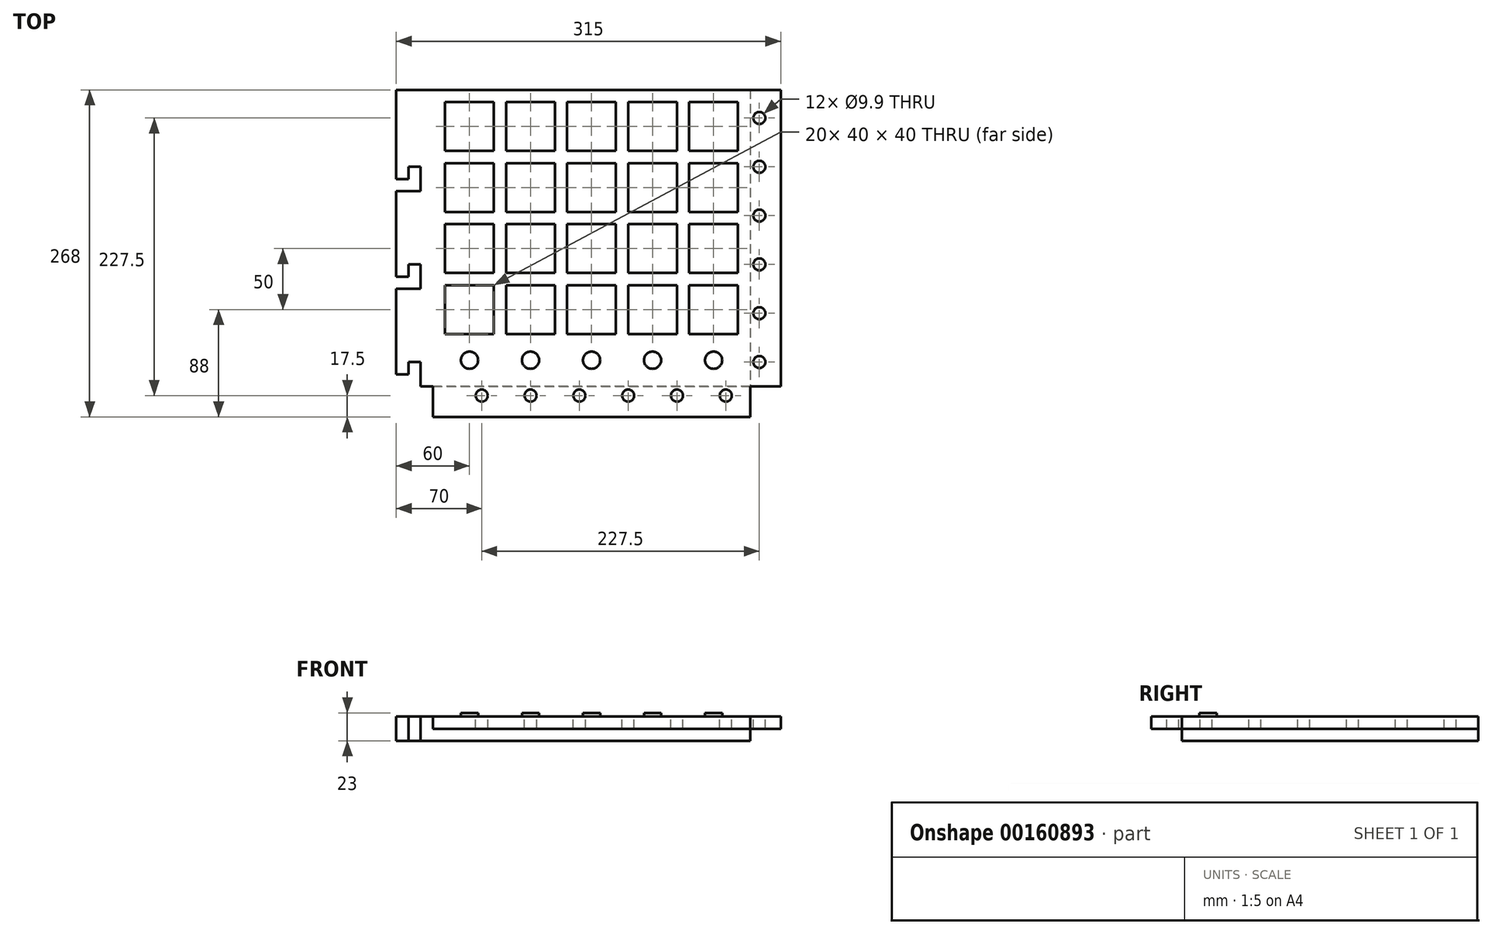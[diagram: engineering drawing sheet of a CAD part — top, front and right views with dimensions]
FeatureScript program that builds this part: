
annotation { "Feature Type Name" : "Feature", "Feature Type Description" : "" }
export const myFeature = defineFeature(function(context is Context, id is Id, definition is map)
    precondition{}
    {
        {
            var Q0;
            Q0=qCreatedBy(makeId("Top.planeOp"),FACE);
            var sketch = newSketch(context, id + "F0", { "sketchPlane" : qUnion([Q0])});
            skLineSegment(sketch, "E0", {"start": v(-205.43, 0) * mm, "end": v(243.02, 0) * mm, "construction": true});
            skLineSegment(sketch, "E1", {"start": v(0, 205.1) * mm, "end": v(0, -211.65) * mm, "construction": true});
            skLineSegment(sketch, "E2.bottom", {"start": v(130, 105) * mm, "end": v(-130, 105) * mm});
            skLineSegment(sketch, "E2.top", {"start": v(130, -105) * mm, "end": v(-130, -105) * mm});
            skLineSegment(sketch, "E2.left", {"start": v(130, 105) * mm, "end": v(130, -105) * mm});
            skLineSegment(sketch, "E2.right", {"start": v(-130, 105) * mm, "end": v(-130, -105) * mm});
            skPoint(sketch, "E2.middle", {"position": v(0, 0) * mm});
            skLineSegment(sketch, "E3.bottom", {"start": v(80, -55) * mm, "end": v(120, -55) * mm});
            skLineSegment(sketch, "E3.top", {"start": v(80, -95) * mm, "end": v(120, -95) * mm});
            skLineSegment(sketch, "E3.left", {"start": v(80, -55) * mm, "end": v(80, -95) * mm});
            skLineSegment(sketch, "E3.right", {"start": v(120, -55) * mm, "end": v(120, -95) * mm});
            skLineSegment(sketch, "E4.0.1.0", {"start": v(80, -5) * mm, "end": v(120, -5) * mm});
            skLineSegment(sketch, "E4.0.1.1", {"start": v(120, -5) * mm, "end": v(120, -45) * mm});
            skLineSegment(sketch, "E4.0.1.2", {"start": v(80, -45) * mm, "end": v(120, -45) * mm});
            skLineSegment(sketch, "E4.0.1.3", {"start": v(80, -5) * mm, "end": v(80, -45) * mm});
            skLineSegment(sketch, "E4.0.2.0", {"start": v(80, 45) * mm, "end": v(120, 45) * mm});
            skLineSegment(sketch, "E4.0.2.1", {"start": v(120, 45) * mm, "end": v(120, 5) * mm});
            skLineSegment(sketch, "E4.0.2.2", {"start": v(80, 5) * mm, "end": v(120, 5) * mm});
            skLineSegment(sketch, "E4.0.2.3", {"start": v(80, 45) * mm, "end": v(80, 5) * mm});
            skLineSegment(sketch, "E4.0.3.0", {"start": v(80, 95) * mm, "end": v(120, 95) * mm});
            skLineSegment(sketch, "E4.0.3.1", {"start": v(120, 95) * mm, "end": v(120, 55) * mm});
            skLineSegment(sketch, "E4.0.3.2", {"start": v(80, 55) * mm, "end": v(120, 55) * mm});
            skLineSegment(sketch, "E4.0.3.3", {"start": v(80, 95) * mm, "end": v(80, 55) * mm});
            skLineSegment(sketch, "E4.1.0.0", {"start": v(30, -55) * mm, "end": v(70, -55) * mm});
            skLineSegment(sketch, "E4.1.0.1", {"start": v(70, -55) * mm, "end": v(70, -95) * mm});
            skLineSegment(sketch, "E4.1.0.2", {"start": v(30, -95) * mm, "end": v(70, -95) * mm});
            skLineSegment(sketch, "E4.1.0.3", {"start": v(30, -55) * mm, "end": v(30, -95) * mm});
            skLineSegment(sketch, "E4.1.1.0", {"start": v(30, -5) * mm, "end": v(70, -5) * mm});
            skLineSegment(sketch, "E4.1.1.1", {"start": v(70, -5) * mm, "end": v(70, -45) * mm});
            skLineSegment(sketch, "E4.1.1.2", {"start": v(30, -45) * mm, "end": v(70, -45) * mm});
            skLineSegment(sketch, "E4.1.1.3", {"start": v(30, -5) * mm, "end": v(30, -45) * mm});
            skLineSegment(sketch, "E4.1.2.0", {"start": v(30, 45) * mm, "end": v(70, 45) * mm});
            skLineSegment(sketch, "E4.1.2.1", {"start": v(70, 45) * mm, "end": v(70, 5) * mm});
            skLineSegment(sketch, "E4.1.2.2", {"start": v(30, 5) * mm, "end": v(70, 5) * mm});
            skLineSegment(sketch, "E4.1.2.3", {"start": v(30, 45) * mm, "end": v(30, 5) * mm});
            skLineSegment(sketch, "E4.1.3.0", {"start": v(30, 95) * mm, "end": v(70, 95) * mm});
            skLineSegment(sketch, "E4.1.3.1", {"start": v(70, 95) * mm, "end": v(70, 55) * mm});
            skLineSegment(sketch, "E4.1.3.2", {"start": v(30, 55) * mm, "end": v(70, 55) * mm});
            skLineSegment(sketch, "E4.1.3.3", {"start": v(30, 95) * mm, "end": v(30, 55) * mm});
            skLineSegment(sketch, "E4.2.0.0", {"start": v(-20, -55) * mm, "end": v(20, -55) * mm});
            skLineSegment(sketch, "E4.2.0.1", {"start": v(20, -55) * mm, "end": v(20, -95) * mm});
            skLineSegment(sketch, "E4.2.0.2", {"start": v(-20, -95) * mm, "end": v(20, -95) * mm});
            skLineSegment(sketch, "E4.2.0.3", {"start": v(-20, -55) * mm, "end": v(-20, -95) * mm});
            skLineSegment(sketch, "E4.2.1.0", {"start": v(-20, -5) * mm, "end": v(20, -5) * mm});
            skLineSegment(sketch, "E4.2.1.1", {"start": v(20, -5) * mm, "end": v(20, -45) * mm});
            skLineSegment(sketch, "E4.2.1.2", {"start": v(-20, -45) * mm, "end": v(20, -45) * mm});
            skLineSegment(sketch, "E4.2.1.3", {"start": v(-20, -5) * mm, "end": v(-20, -45) * mm});
            skLineSegment(sketch, "E4.2.2.0", {"start": v(-20, 45) * mm, "end": v(20, 45) * mm});
            skLineSegment(sketch, "E4.2.2.1", {"start": v(20, 45) * mm, "end": v(20, 5) * mm});
            skLineSegment(sketch, "E4.2.2.2", {"start": v(-20, 5) * mm, "end": v(20, 5) * mm});
            skLineSegment(sketch, "E4.2.2.3", {"start": v(-20, 45) * mm, "end": v(-20, 5) * mm});
            skLineSegment(sketch, "E4.2.3.0", {"start": v(-20, 95) * mm, "end": v(20, 95) * mm});
            skLineSegment(sketch, "E4.2.3.1", {"start": v(20, 95) * mm, "end": v(20, 55) * mm});
            skLineSegment(sketch, "E4.2.3.2", {"start": v(-20, 55) * mm, "end": v(20, 55) * mm});
            skLineSegment(sketch, "E4.2.3.3", {"start": v(-20, 95) * mm, "end": v(-20, 55) * mm});
            skLineSegment(sketch, "E4.3.0.0", {"start": v(-70, -55) * mm, "end": v(-30, -55) * mm});
            skLineSegment(sketch, "E4.3.0.1", {"start": v(-30, -55) * mm, "end": v(-30, -95) * mm});
            skLineSegment(sketch, "E4.3.0.2", {"start": v(-70, -95) * mm, "end": v(-30, -95) * mm});
            skLineSegment(sketch, "E4.3.0.3", {"start": v(-70, -55) * mm, "end": v(-70, -95) * mm});
            skLineSegment(sketch, "E4.3.1.0", {"start": v(-70, -5) * mm, "end": v(-30, -5) * mm});
            skLineSegment(sketch, "E4.3.1.1", {"start": v(-30, -5) * mm, "end": v(-30, -45) * mm});
            skLineSegment(sketch, "E4.3.1.2", {"start": v(-70, -45) * mm, "end": v(-30, -45) * mm});
            skLineSegment(sketch, "E4.3.1.3", {"start": v(-70, -5) * mm, "end": v(-70, -45) * mm});
            skLineSegment(sketch, "E4.3.2.0", {"start": v(-70, 45) * mm, "end": v(-30, 45) * mm});
            skLineSegment(sketch, "E4.3.2.1", {"start": v(-30, 45) * mm, "end": v(-30, 5) * mm});
            skLineSegment(sketch, "E4.3.2.2", {"start": v(-70, 5) * mm, "end": v(-30, 5) * mm});
            skLineSegment(sketch, "E4.3.2.3", {"start": v(-70, 45) * mm, "end": v(-70, 5) * mm});
            skLineSegment(sketch, "E4.3.3.0", {"start": v(-70, 95) * mm, "end": v(-30, 95) * mm});
            skLineSegment(sketch, "E4.3.3.1", {"start": v(-30, 95) * mm, "end": v(-30, 55) * mm});
            skLineSegment(sketch, "E4.3.3.2", {"start": v(-70, 55) * mm, "end": v(-30, 55) * mm});
            skLineSegment(sketch, "E4.3.3.3", {"start": v(-70, 95) * mm, "end": v(-70, 55) * mm});
            skLineSegment(sketch, "E4.4.0.0", {"start": v(-120, -55) * mm, "end": v(-80, -55) * mm});
            skLineSegment(sketch, "E4.4.0.1", {"start": v(-80, -55) * mm, "end": v(-80, -95) * mm});
            skLineSegment(sketch, "E4.4.0.2", {"start": v(-120, -95) * mm, "end": v(-80, -95) * mm});
            skLineSegment(sketch, "E4.4.0.3", {"start": v(-120, -55) * mm, "end": v(-120, -95) * mm});
            skLineSegment(sketch, "E4.4.1.0", {"start": v(-120, -5) * mm, "end": v(-80, -5) * mm});
            skLineSegment(sketch, "E4.4.1.1", {"start": v(-80, -5) * mm, "end": v(-80, -45) * mm});
            skLineSegment(sketch, "E4.4.1.2", {"start": v(-120, -45) * mm, "end": v(-80, -45) * mm});
            skLineSegment(sketch, "E4.4.1.3", {"start": v(-120, -5) * mm, "end": v(-120, -45) * mm});
            skLineSegment(sketch, "E4.4.2.0", {"start": v(-120, 45) * mm, "end": v(-80, 45) * mm});
            skLineSegment(sketch, "E4.4.2.1", {"start": v(-80, 45) * mm, "end": v(-80, 5) * mm});
            skLineSegment(sketch, "E4.4.2.2", {"start": v(-120, 5) * mm, "end": v(-80, 5) * mm});
            skLineSegment(sketch, "E4.4.2.3", {"start": v(-120, 45) * mm, "end": v(-120, 5) * mm});
            skLineSegment(sketch, "E4.4.3.0", {"start": v(-120, 95) * mm, "end": v(-80, 95) * mm});
            skLineSegment(sketch, "E4.4.3.1", {"start": v(-80, 95) * mm, "end": v(-80, 55) * mm});
            skLineSegment(sketch, "E4.4.3.2", {"start": v(-120, 55) * mm, "end": v(-80, 55) * mm});
            skLineSegment(sketch, "E4.4.3.3", {"start": v(-120, 95) * mm, "end": v(-120, 55) * mm});
            skLineSegment(sketch, "E4.direction1", {"start": v(80, -95) * mm, "end": v(30, -95) * mm, "construction": true});
            skLineSegment(sketch, "E4.direction2", {"start": v(80, -95) * mm, "end": v(80, -45) * mm, "construction": true});
            skSolve(sketch);
        }
        {
            var Q0;
            Q0 = qSketchRegion(id + "F0", true);
            extrude(context, id + "F1", {"entities" : qUnion([Q0]), "depth" : 20 * mm});
        }
        {
            var Q0;
            Q0=makeQuery(id+"F1.opExtrude","SWEPT_FACE",FACE,{"disambiguationData":[OSD([sQuery(id+"F0.wireOp",EDGE,"E2.top")])]});
            extrude(context, id + "F2", {"entities" : qUnion([Q0]), "operationType" : NewBodyOperationType.ADD, "depth" : 33 * mm});
        }
        {
            var Q0;
            Q0=makeQuery(id+"F2.opExtrude","CAP_FACE",FACE,{"disambiguationData":[OSD([sQuery(id+"F0.wireOp",EDGE,"E2.top")])],"isStart":false});
            var sketch = newSketch(context, id + "F3", { "sketchPlane" : qUnion([Q0])});
            skLineSegment(sketch, "E5.bottom", {"start": v(-130, 20) * mm, "end": v(130, 20) * mm});
            skLineSegment(sketch, "E5.top", {"start": v(-130, 10) * mm, "end": v(130, 10) * mm});
            skLineSegment(sketch, "E5.left", {"start": v(-130, 20) * mm, "end": v(-130, 10) * mm});
            skLineSegment(sketch, "E5.right", {"start": v(130, 20) * mm, "end": v(130, 10) * mm});
            skSolve(sketch);
        }
        {
            var Q0;
            Q0 = qSketchRegion(id + "F3", true);
            extrude(context, id + "F4", {"entities" : qUnion([Q0]), "operationType" : NewBodyOperationType.ADD, "depth" : 25 * mm});
        }
        {
            var Q0;
            {var subQ0=sQuery(id+"F0.wireOp",EDGE,"E2.top");Q0=makeQuery(id+"F4.boolean.opBoolean","MERGE",FACE,{"derivedFrom":[makeQuery(id+"F2.boolean.opBoolean","MERGE",FACE,{"derivedFrom":[makeQuery(id+"F1.opExtrude","CAP_FACE",FACE,{"disambiguationData":[OSD([sQuery(id+"F0.wireOp",EDGE,"E2.bottom"),subQ0,sQuery(id+"F0.wireOp",EDGE,"E2.left"),sQuery(id+"F0.wireOp",EDGE,"E2.right"),sQuery(id+"F0.wireOp",EDGE,"E3.bottom"),sQuery(id+"F0.wireOp",EDGE,"E3.top"),sQuery(id+"F0.wireOp",EDGE,"E3.left"),sQuery(id+"F0.wireOp",EDGE,"E3.right"),sQuery(id+"F0.wireOp",EDGE,"E4.0.1.0"),sQuery(id+"F0.wireOp",EDGE,"E4.0.1.1"),sQuery(id+"F0.wireOp",EDGE,"E4.0.1.2"),sQuery(id+"F0.wireOp",EDGE,"E4.0.1.3"),sQuery(id+"F0.wireOp",EDGE,"E4.0.2.0"),sQuery(id+"F0.wireOp",EDGE,"E4.0.2.1"),sQuery(id+"F0.wireOp",EDGE,"E4.0.2.2"),sQuery(id+"F0.wireOp",EDGE,"E4.0.2.3"),sQuery(id+"F0.wireOp",EDGE,"E4.0.3.0"),sQuery(id+"F0.wireOp",EDGE,"E4.0.3.1"),sQuery(id+"F0.wireOp",EDGE,"E4.0.3.2"),sQuery(id+"F0.wireOp",EDGE,"E4.0.3.3"),sQuery(id+"F0.wireOp",EDGE,"E4.1.0.0"),sQuery(id+"F0.wireOp",EDGE,"E4.1.0.1"),sQuery(id+"F0.wireOp",EDGE,"E4.1.0.2"),sQuery(id+"F0.wireOp",EDGE,"E4.1.0.3"),sQuery(id+"F0.wireOp",EDGE,"E4.1.1.0"),sQuery(id+"F0.wireOp",EDGE,"E4.1.1.1"),sQuery(id+"F0.wireOp",EDGE,"E4.1.1.2"),sQuery(id+"F0.wireOp",EDGE,"E4.1.1.3"),sQuery(id+"F0.wireOp",EDGE,"E4.1.2.0"),sQuery(id+"F0.wireOp",EDGE,"E4.1.2.1"),sQuery(id+"F0.wireOp",EDGE,"E4.1.2.2"),sQuery(id+"F0.wireOp",EDGE,"E4.1.2.3"),sQuery(id+"F0.wireOp",EDGE,"E4.1.3.0"),sQuery(id+"F0.wireOp",EDGE,"E4.1.3.1"),sQuery(id+"F0.wireOp",EDGE,"E4.1.3.2"),sQuery(id+"F0.wireOp",EDGE,"E4.1.3.3"),sQuery(id+"F0.wireOp",EDGE,"E4.2.0.0"),sQuery(id+"F0.wireOp",EDGE,"E4.2.0.1"),sQuery(id+"F0.wireOp",EDGE,"E4.2.0.2"),sQuery(id+"F0.wireOp",EDGE,"E4.2.0.3"),sQuery(id+"F0.wireOp",EDGE,"E4.2.1.0"),sQuery(id+"F0.wireOp",EDGE,"E4.2.1.1"),sQuery(id+"F0.wireOp",EDGE,"E4.2.1.2"),sQuery(id+"F0.wireOp",EDGE,"E4.2.1.3"),sQuery(id+"F0.wireOp",EDGE,"E4.2.2.0"),sQuery(id+"F0.wireOp",EDGE,"E4.2.2.1"),sQuery(id+"F0.wireOp",EDGE,"E4.2.2.2"),sQuery(id+"F0.wireOp",EDGE,"E4.2.2.3"),sQuery(id+"F0.wireOp",EDGE,"E4.2.3.0"),sQuery(id+"F0.wireOp",EDGE,"E4.2.3.1"),sQuery(id+"F0.wireOp",EDGE,"E4.2.3.2"),sQuery(id+"F0.wireOp",EDGE,"E4.2.3.3"),sQuery(id+"F0.wireOp",EDGE,"E4.3.0.0"),sQuery(id+"F0.wireOp",EDGE,"E4.3.0.1"),sQuery(id+"F0.wireOp",EDGE,"E4.3.0.2"),sQuery(id+"F0.wireOp",EDGE,"E4.3.0.3"),sQuery(id+"F0.wireOp",EDGE,"E4.3.1.0"),sQuery(id+"F0.wireOp",EDGE,"E4.3.1.1"),sQuery(id+"F0.wireOp",EDGE,"E4.3.1.2"),sQuery(id+"F0.wireOp",EDGE,"E4.3.1.3"),sQuery(id+"F0.wireOp",EDGE,"E4.3.2.0"),sQuery(id+"F0.wireOp",EDGE,"E4.3.2.1"),sQuery(id+"F0.wireOp",EDGE,"E4.3.2.2"),sQuery(id+"F0.wireOp",EDGE,"E4.3.2.3"),sQuery(id+"F0.wireOp",EDGE,"E4.3.3.0"),sQuery(id+"F0.wireOp",EDGE,"E4.3.3.1"),sQuery(id+"F0.wireOp",EDGE,"E4.3.3.2"),sQuery(id+"F0.wireOp",EDGE,"E4.3.3.3"),sQuery(id+"F0.wireOp",EDGE,"E4.4.0.0"),sQuery(id+"F0.wireOp",EDGE,"E4.4.0.1"),sQuery(id+"F0.wireOp",EDGE,"E4.4.0.2"),sQuery(id+"F0.wireOp",EDGE,"E4.4.0.3"),sQuery(id+"F0.wireOp",EDGE,"E4.4.1.0"),sQuery(id+"F0.wireOp",EDGE,"E4.4.1.1"),sQuery(id+"F0.wireOp",EDGE,"E4.4.1.2"),sQuery(id+"F0.wireOp",EDGE,"E4.4.1.3"),sQuery(id+"F0.wireOp",EDGE,"E4.4.2.0"),sQuery(id+"F0.wireOp",EDGE,"E4.4.2.1"),sQuery(id+"F0.wireOp",EDGE,"E4.4.2.2"),sQuery(id+"F0.wireOp",EDGE,"E4.4.2.3"),sQuery(id+"F0.wireOp",EDGE,"E4.4.3.0"),sQuery(id+"F0.wireOp",EDGE,"E4.4.3.1"),sQuery(id+"F0.wireOp",EDGE,"E4.4.3.2"),sQuery(id+"F0.wireOp",EDGE,"E4.4.3.3")])],"isStart":false}),makeQuery(id+"F2.opExtrude","SWEPT_FACE",FACE,{"disambiguationData":[OSD([subQ0]),TDD([makeQuery(id+"F1.opExtrude","CAP_EDGE",EDGE,{"disambiguationData":[OSD([subQ0])],"isStart":false})])]})]}),makeQuery(id+"F4.opExtrude","SWEPT_FACE",FACE,{"disambiguationData":[OSD([sQuery(id+"F3.wireOp",EDGE,"E5.bottom")])]})]});}
            var sketch = newSketch(context, id + "F5", { "sketchPlane" : qUnion([Q0])});
            skCircle(sketch, "E6", {"center": v(110, -145.5) * mm, "radius": 4.95 * mm});
            skLineSegment(sketch, "E7", {"start": v(-121.54, -145.5) * mm, "end": v(178.6, -145.5) * mm, "construction": true});
            skLineSegment(sketch, "E8", {"start": v(110, -159.43) * mm, "end": v(110, -131.93) * mm, "construction": true});
            skCircle(sketch, "E9.1.0.0", {"center": v(70, -145.5) * mm, "radius": 4.95 * mm});
            skCircle(sketch, "E9.2.0.0", {"center": v(30, -145.5) * mm, "radius": 4.95 * mm});
            skCircle(sketch, "E9.3.0.0", {"center": v(-10, -145.5) * mm, "radius": 4.95 * mm});
            skCircle(sketch, "E9.4.0.0", {"center": v(-50, -145.5) * mm, "radius": 4.95 * mm});
            skCircle(sketch, "E9.5.0.0", {"center": v(-90, -145.5) * mm, "radius": 4.95 * mm});
            skLineSegment(sketch, "E9.direction1", {"start": v(110, -145.5) * mm, "end": v(70, -145.5) * mm, "construction": true});
            skSolve(sketch);
        }
        {
            var Q0;
            Q0 = qSketchRegion(id + "F5", true);
            extrude(context, id + "F6", {"entities" : qUnion([Q0]), "operationType" : NewBodyOperationType.REMOVE, "oppositeDirection" : true, "depth" : 25 * mm});
        }
        {
            var Q0;
            {var subQ0=sQuery(id+"F0.wireOp",EDGE,"E2.left");Q0=makeQuery(id+"F4.boolean.opBoolean","MERGE",FACE,{"derivedFrom":[makeQuery(id+"F2.boolean.opBoolean","MERGE",FACE,{"derivedFrom":[makeQuery(id+"F1.opExtrude","SWEPT_FACE",FACE,{"disambiguationData":[OSD([subQ0])]}),makeQuery(id+"F2.opExtrude","SWEPT_FACE",FACE,{"disambiguationData":[OSD([sQuery(id+"F0.wireOp",EDGE,"E2.top"),subQ0])]})]}),makeQuery(id+"F4.opExtrude","SWEPT_FACE",FACE,{"disambiguationData":[OSD([sQuery(id+"F3.wireOp",EDGE,"E5.right")])]})]});}
            var sketch = newSketch(context, id + "F7", { "sketchPlane" : qUnion([Q0])});
            skLineSegment(sketch, "E10.bottom", {"start": v(105, 20) * mm, "end": v(-138, 20) * mm});
            skLineSegment(sketch, "E10.top", {"start": v(105, 10) * mm, "end": v(-138, 10) * mm});
            skLineSegment(sketch, "E10.left", {"start": v(105, 20) * mm, "end": v(105, 10) * mm});
            skLineSegment(sketch, "E10.right", {"start": v(-138, 20) * mm, "end": v(-138, 10) * mm});
            skSolve(sketch);
        }
        {
            var Q0;
            Q0 = qSketchRegion(id + "F7", true);
            extrude(context, id + "F8", {"entities" : qUnion([Q0]), "operationType" : NewBodyOperationType.ADD, "depth" : 25 * mm});
        }
        {
            var Q0;
            {var subQ0=sQuery(id+"F0.wireOp",EDGE,"E2.top");Q0=makeQuery(id+"F8.boolean.opBoolean","MERGE",FACE,{"derivedFrom":[makeQuery(id+"F4.boolean.opBoolean","MERGE",FACE,{"derivedFrom":[makeQuery(id+"F2.boolean.opBoolean","MERGE",FACE,{"derivedFrom":[makeQuery(id+"F1.opExtrude","CAP_FACE",FACE,{"disambiguationData":[OSD([sQuery(id+"F0.wireOp",EDGE,"E2.bottom"),subQ0,sQuery(id+"F0.wireOp",EDGE,"E2.left"),sQuery(id+"F0.wireOp",EDGE,"E2.right"),sQuery(id+"F0.wireOp",EDGE,"E3.bottom"),sQuery(id+"F0.wireOp",EDGE,"E3.top"),sQuery(id+"F0.wireOp",EDGE,"E3.left"),sQuery(id+"F0.wireOp",EDGE,"E3.right"),sQuery(id+"F0.wireOp",EDGE,"E4.0.1.0"),sQuery(id+"F0.wireOp",EDGE,"E4.0.1.1"),sQuery(id+"F0.wireOp",EDGE,"E4.0.1.2"),sQuery(id+"F0.wireOp",EDGE,"E4.0.1.3"),sQuery(id+"F0.wireOp",EDGE,"E4.0.2.0"),sQuery(id+"F0.wireOp",EDGE,"E4.0.2.1"),sQuery(id+"F0.wireOp",EDGE,"E4.0.2.2"),sQuery(id+"F0.wireOp",EDGE,"E4.0.2.3"),sQuery(id+"F0.wireOp",EDGE,"E4.0.3.0"),sQuery(id+"F0.wireOp",EDGE,"E4.0.3.1"),sQuery(id+"F0.wireOp",EDGE,"E4.0.3.2"),sQuery(id+"F0.wireOp",EDGE,"E4.0.3.3"),sQuery(id+"F0.wireOp",EDGE,"E4.1.0.0"),sQuery(id+"F0.wireOp",EDGE,"E4.1.0.1"),sQuery(id+"F0.wireOp",EDGE,"E4.1.0.2"),sQuery(id+"F0.wireOp",EDGE,"E4.1.0.3"),sQuery(id+"F0.wireOp",EDGE,"E4.1.1.0"),sQuery(id+"F0.wireOp",EDGE,"E4.1.1.1"),sQuery(id+"F0.wireOp",EDGE,"E4.1.1.2"),sQuery(id+"F0.wireOp",EDGE,"E4.1.1.3"),sQuery(id+"F0.wireOp",EDGE,"E4.1.2.0"),sQuery(id+"F0.wireOp",EDGE,"E4.1.2.1"),sQuery(id+"F0.wireOp",EDGE,"E4.1.2.2"),sQuery(id+"F0.wireOp",EDGE,"E4.1.2.3"),sQuery(id+"F0.wireOp",EDGE,"E4.1.3.0"),sQuery(id+"F0.wireOp",EDGE,"E4.1.3.1"),sQuery(id+"F0.wireOp",EDGE,"E4.1.3.2"),sQuery(id+"F0.wireOp",EDGE,"E4.1.3.3"),sQuery(id+"F0.wireOp",EDGE,"E4.2.0.0"),sQuery(id+"F0.wireOp",EDGE,"E4.2.0.1"),sQuery(id+"F0.wireOp",EDGE,"E4.2.0.2"),sQuery(id+"F0.wireOp",EDGE,"E4.2.0.3"),sQuery(id+"F0.wireOp",EDGE,"E4.2.1.0"),sQuery(id+"F0.wireOp",EDGE,"E4.2.1.1"),sQuery(id+"F0.wireOp",EDGE,"E4.2.1.2"),sQuery(id+"F0.wireOp",EDGE,"E4.2.1.3"),sQuery(id+"F0.wireOp",EDGE,"E4.2.2.0"),sQuery(id+"F0.wireOp",EDGE,"E4.2.2.1"),sQuery(id+"F0.wireOp",EDGE,"E4.2.2.2"),sQuery(id+"F0.wireOp",EDGE,"E4.2.2.3"),sQuery(id+"F0.wireOp",EDGE,"E4.2.3.0"),sQuery(id+"F0.wireOp",EDGE,"E4.2.3.1"),sQuery(id+"F0.wireOp",EDGE,"E4.2.3.2"),sQuery(id+"F0.wireOp",EDGE,"E4.2.3.3"),sQuery(id+"F0.wireOp",EDGE,"E4.3.0.0"),sQuery(id+"F0.wireOp",EDGE,"E4.3.0.1"),sQuery(id+"F0.wireOp",EDGE,"E4.3.0.2"),sQuery(id+"F0.wireOp",EDGE,"E4.3.0.3"),sQuery(id+"F0.wireOp",EDGE,"E4.3.1.0"),sQuery(id+"F0.wireOp",EDGE,"E4.3.1.1"),sQuery(id+"F0.wireOp",EDGE,"E4.3.1.2"),sQuery(id+"F0.wireOp",EDGE,"E4.3.1.3"),sQuery(id+"F0.wireOp",EDGE,"E4.3.2.0"),sQuery(id+"F0.wireOp",EDGE,"E4.3.2.1"),sQuery(id+"F0.wireOp",EDGE,"E4.3.2.2"),sQuery(id+"F0.wireOp",EDGE,"E4.3.2.3"),sQuery(id+"F0.wireOp",EDGE,"E4.3.3.0"),sQuery(id+"F0.wireOp",EDGE,"E4.3.3.1"),sQuery(id+"F0.wireOp",EDGE,"E4.3.3.2"),sQuery(id+"F0.wireOp",EDGE,"E4.3.3.3"),sQuery(id+"F0.wireOp",EDGE,"E4.4.0.0"),sQuery(id+"F0.wireOp",EDGE,"E4.4.0.1"),sQuery(id+"F0.wireOp",EDGE,"E4.4.0.2"),sQuery(id+"F0.wireOp",EDGE,"E4.4.0.3"),sQuery(id+"F0.wireOp",EDGE,"E4.4.1.0"),sQuery(id+"F0.wireOp",EDGE,"E4.4.1.1"),sQuery(id+"F0.wireOp",EDGE,"E4.4.1.2"),sQuery(id+"F0.wireOp",EDGE,"E4.4.1.3"),sQuery(id+"F0.wireOp",EDGE,"E4.4.2.0"),sQuery(id+"F0.wireOp",EDGE,"E4.4.2.1"),sQuery(id+"F0.wireOp",EDGE,"E4.4.2.2"),sQuery(id+"F0.wireOp",EDGE,"E4.4.2.3"),sQuery(id+"F0.wireOp",EDGE,"E4.4.3.0"),sQuery(id+"F0.wireOp",EDGE,"E4.4.3.1"),sQuery(id+"F0.wireOp",EDGE,"E4.4.3.2"),sQuery(id+"F0.wireOp",EDGE,"E4.4.3.3")])],"isStart":false}),makeQuery(id+"F2.opExtrude","SWEPT_FACE",FACE,{"disambiguationData":[OSD([subQ0]),TDD([makeQuery(id+"F1.opExtrude","CAP_EDGE",EDGE,{"disambiguationData":[OSD([subQ0])],"isStart":false})])]})]}),makeQuery(id+"F4.opExtrude","SWEPT_FACE",FACE,{"disambiguationData":[OSD([sQuery(id+"F3.wireOp",EDGE,"E5.bottom")])]})]}),makeQuery(id+"F8.opExtrude","SWEPT_FACE",FACE,{"disambiguationData":[OSD([sQuery(id+"F7.wireOp",EDGE,"E10.bottom")])]})]});}
            var sketch = newSketch(context, id + "F9", { "sketchPlane" : qUnion([Q0])});
            skLineSegment(sketch, "E11", {"start": v(137.5, -148.15) * mm, "end": v(137.5, 118.27) * mm, "construction": true});
            skCircle(sketch, "E12", {"center": v(137.5, -118) * mm, "radius": 4.95 * mm});
            skLineSegment(sketch, "E13", {"start": v(128.57, -118) * mm, "end": v(148.12, -118) * mm, "construction": true});
            skCircle(sketch, "E14.0.1.0", {"center": v(137.5, -78) * mm, "radius": 4.95 * mm});
            skCircle(sketch, "E14.0.2.0", {"center": v(137.5, -38) * mm, "radius": 4.95 * mm});
            skCircle(sketch, "E14.0.3.0", {"center": v(137.5, 2) * mm, "radius": 4.95 * mm});
            skCircle(sketch, "E14.0.4.0", {"center": v(137.5, 42) * mm, "radius": 4.95 * mm});
            skCircle(sketch, "E14.0.5.0", {"center": v(137.5, 82) * mm, "radius": 4.95 * mm});
            skLineSegment(sketch, "E14.direction1", {"start": v(137.5, -118) * mm, "end": v(150.25, -118) * mm, "construction": true});
            skLineSegment(sketch, "E14.direction2", {"start": v(137.5, -118) * mm, "end": v(137.5, -78) * mm, "construction": true});
            skSolve(sketch);
        }
        {
            var Q0;
            Q0 = qSketchRegion(id + "F9", true);
            extrude(context, id + "F10", {"entities" : qUnion([Q0]), "operationType" : NewBodyOperationType.REMOVE, "oppositeDirection" : true, "depth" : 25 * mm});
        }
        {
            var Q0;
            {var subQ0=sQuery(id+"F0.wireOp",EDGE,"E2.right");Q0=makeQuery(id+"F4.boolean.opBoolean","MERGE",FACE,{"derivedFrom":[makeQuery(id+"F2.boolean.opBoolean","MERGE",FACE,{"derivedFrom":[makeQuery(id+"F1.opExtrude","SWEPT_FACE",FACE,{"disambiguationData":[OSD([subQ0])]}),makeQuery(id+"F2.opExtrude","SWEPT_FACE",FACE,{"disambiguationData":[OSD([sQuery(id+"F0.wireOp",EDGE,"E2.top"),subQ0])]})]}),makeQuery(id+"F4.opExtrude","SWEPT_FACE",FACE,{"disambiguationData":[OSD([sQuery(id+"F3.wireOp",EDGE,"E5.left")])]})]});}
            var sketch = newSketch(context, id + "F11", { "sketchPlane" : qUnion([Q0])});
            skLineSegment(sketch, "E15.bottom", {"start": v(-105, 20) * mm, "end": v(138, 20) * mm});
            skLineSegment(sketch, "E15.top", {"start": v(-105, 0) * mm, "end": v(138, 0) * mm});
            skLineSegment(sketch, "E15.left", {"start": v(-105, 20) * mm, "end": v(-105, 0) * mm});
            skLineSegment(sketch, "E15.right", {"start": v(138, 20) * mm, "end": v(138, 0) * mm});
            skSolve(sketch);
        }
        {
            var Q0;
            Q0 = qSketchRegion(id + "F11", true);
            extrude(context, id + "F12", {"entities" : qUnion([Q0]), "operationType" : NewBodyOperationType.ADD, "depth" : 30 * mm});
        }
        {
            var Q0;
            {var subQ0=sQuery(id+"F0.wireOp",EDGE,"E2.top");Q0=makeQuery(id+"F12.boolean.opBoolean","MERGE",FACE,{"derivedFrom":[makeQuery(id+"F8.boolean.opBoolean","MERGE",FACE,{"derivedFrom":[makeQuery(id+"F4.boolean.opBoolean","MERGE",FACE,{"derivedFrom":[makeQuery(id+"F2.boolean.opBoolean","MERGE",FACE,{"derivedFrom":[makeQuery(id+"F1.opExtrude","CAP_FACE",FACE,{"disambiguationData":[OSD([sQuery(id+"F0.wireOp",EDGE,"E2.bottom"),subQ0,sQuery(id+"F0.wireOp",EDGE,"E2.left"),sQuery(id+"F0.wireOp",EDGE,"E2.right"),sQuery(id+"F0.wireOp",EDGE,"E3.bottom"),sQuery(id+"F0.wireOp",EDGE,"E3.top"),sQuery(id+"F0.wireOp",EDGE,"E3.left"),sQuery(id+"F0.wireOp",EDGE,"E3.right"),sQuery(id+"F0.wireOp",EDGE,"E4.0.1.0"),sQuery(id+"F0.wireOp",EDGE,"E4.0.1.1"),sQuery(id+"F0.wireOp",EDGE,"E4.0.1.2"),sQuery(id+"F0.wireOp",EDGE,"E4.0.1.3"),sQuery(id+"F0.wireOp",EDGE,"E4.0.2.0"),sQuery(id+"F0.wireOp",EDGE,"E4.0.2.1"),sQuery(id+"F0.wireOp",EDGE,"E4.0.2.2"),sQuery(id+"F0.wireOp",EDGE,"E4.0.2.3"),sQuery(id+"F0.wireOp",EDGE,"E4.0.3.0"),sQuery(id+"F0.wireOp",EDGE,"E4.0.3.1"),sQuery(id+"F0.wireOp",EDGE,"E4.0.3.2"),sQuery(id+"F0.wireOp",EDGE,"E4.0.3.3"),sQuery(id+"F0.wireOp",EDGE,"E4.1.0.0"),sQuery(id+"F0.wireOp",EDGE,"E4.1.0.1"),sQuery(id+"F0.wireOp",EDGE,"E4.1.0.2"),sQuery(id+"F0.wireOp",EDGE,"E4.1.0.3"),sQuery(id+"F0.wireOp",EDGE,"E4.1.1.0"),sQuery(id+"F0.wireOp",EDGE,"E4.1.1.1"),sQuery(id+"F0.wireOp",EDGE,"E4.1.1.2"),sQuery(id+"F0.wireOp",EDGE,"E4.1.1.3"),sQuery(id+"F0.wireOp",EDGE,"E4.1.2.0"),sQuery(id+"F0.wireOp",EDGE,"E4.1.2.1"),sQuery(id+"F0.wireOp",EDGE,"E4.1.2.2"),sQuery(id+"F0.wireOp",EDGE,"E4.1.2.3"),sQuery(id+"F0.wireOp",EDGE,"E4.1.3.0"),sQuery(id+"F0.wireOp",EDGE,"E4.1.3.1"),sQuery(id+"F0.wireOp",EDGE,"E4.1.3.2"),sQuery(id+"F0.wireOp",EDGE,"E4.1.3.3"),sQuery(id+"F0.wireOp",EDGE,"E4.2.0.0"),sQuery(id+"F0.wireOp",EDGE,"E4.2.0.1"),sQuery(id+"F0.wireOp",EDGE,"E4.2.0.2"),sQuery(id+"F0.wireOp",EDGE,"E4.2.0.3"),sQuery(id+"F0.wireOp",EDGE,"E4.2.1.0"),sQuery(id+"F0.wireOp",EDGE,"E4.2.1.1"),sQuery(id+"F0.wireOp",EDGE,"E4.2.1.2"),sQuery(id+"F0.wireOp",EDGE,"E4.2.1.3"),sQuery(id+"F0.wireOp",EDGE,"E4.2.2.0"),sQuery(id+"F0.wireOp",EDGE,"E4.2.2.1"),sQuery(id+"F0.wireOp",EDGE,"E4.2.2.2"),sQuery(id+"F0.wireOp",EDGE,"E4.2.2.3"),sQuery(id+"F0.wireOp",EDGE,"E4.2.3.0"),sQuery(id+"F0.wireOp",EDGE,"E4.2.3.1"),sQuery(id+"F0.wireOp",EDGE,"E4.2.3.2"),sQuery(id+"F0.wireOp",EDGE,"E4.2.3.3"),sQuery(id+"F0.wireOp",EDGE,"E4.3.0.0"),sQuery(id+"F0.wireOp",EDGE,"E4.3.0.1"),sQuery(id+"F0.wireOp",EDGE,"E4.3.0.2"),sQuery(id+"F0.wireOp",EDGE,"E4.3.0.3"),sQuery(id+"F0.wireOp",EDGE,"E4.3.1.0"),sQuery(id+"F0.wireOp",EDGE,"E4.3.1.1"),sQuery(id+"F0.wireOp",EDGE,"E4.3.1.2"),sQuery(id+"F0.wireOp",EDGE,"E4.3.1.3"),sQuery(id+"F0.wireOp",EDGE,"E4.3.2.0"),sQuery(id+"F0.wireOp",EDGE,"E4.3.2.1"),sQuery(id+"F0.wireOp",EDGE,"E4.3.2.2"),sQuery(id+"F0.wireOp",EDGE,"E4.3.2.3"),sQuery(id+"F0.wireOp",EDGE,"E4.3.3.0"),sQuery(id+"F0.wireOp",EDGE,"E4.3.3.1"),sQuery(id+"F0.wireOp",EDGE,"E4.3.3.2"),sQuery(id+"F0.wireOp",EDGE,"E4.3.3.3"),sQuery(id+"F0.wireOp",EDGE,"E4.4.0.0"),sQuery(id+"F0.wireOp",EDGE,"E4.4.0.1"),sQuery(id+"F0.wireOp",EDGE,"E4.4.0.2"),sQuery(id+"F0.wireOp",EDGE,"E4.4.0.3"),sQuery(id+"F0.wireOp",EDGE,"E4.4.1.0"),sQuery(id+"F0.wireOp",EDGE,"E4.4.1.1"),sQuery(id+"F0.wireOp",EDGE,"E4.4.1.2"),sQuery(id+"F0.wireOp",EDGE,"E4.4.1.3"),sQuery(id+"F0.wireOp",EDGE,"E4.4.2.0"),sQuery(id+"F0.wireOp",EDGE,"E4.4.2.1"),sQuery(id+"F0.wireOp",EDGE,"E4.4.2.2"),sQuery(id+"F0.wireOp",EDGE,"E4.4.2.3"),sQuery(id+"F0.wireOp",EDGE,"E4.4.3.0"),sQuery(id+"F0.wireOp",EDGE,"E4.4.3.1"),sQuery(id+"F0.wireOp",EDGE,"E4.4.3.2"),sQuery(id+"F0.wireOp",EDGE,"E4.4.3.3")])],"isStart":false}),makeQuery(id+"F2.opExtrude","SWEPT_FACE",FACE,{"disambiguationData":[OSD([subQ0]),TDD([makeQuery(id+"F1.opExtrude","CAP_EDGE",EDGE,{"disambiguationData":[OSD([subQ0])],"isStart":false})])]})]}),makeQuery(id+"F4.opExtrude","SWEPT_FACE",FACE,{"disambiguationData":[OSD([sQuery(id+"F3.wireOp",EDGE,"E5.bottom")])]})]}),makeQuery(id+"F8.opExtrude","SWEPT_FACE",FACE,{"disambiguationData":[OSD([sQuery(id+"F7.wireOp",EDGE,"E10.bottom")])]})]}),makeQuery(id+"F12.opExtrude","SWEPT_FACE",FACE,{"disambiguationData":[OSD([sQuery(id+"F11.wireOp",EDGE,"E15.bottom")])]})]});}
            var sketch = newSketch(context, id + "F13", { "sketchPlane" : qUnion([Q0])});
            skLineSegment(sketch, "E16", {"start": v(-160, -138) * mm, "end": v(-160, -128) * mm});
            skLineSegment(sketch, "E17", {"start": v(-160, -128) * mm, "end": v(-150, -128) * mm});
            skLineSegment(sketch, "E18", {"start": v(-150, -128) * mm, "end": v(-150, -118) * mm});
            skLineSegment(sketch, "E19", {"start": v(-150, -118) * mm, "end": v(-140, -118) * mm});
            skLineSegment(sketch, "E20", {"start": v(-140, -118) * mm, "end": v(-140, -138) * mm});
            skLineSegment(sketch, "E21", {"start": v(-140, -138) * mm, "end": v(-160, -138) * mm});
            skLineSegment(sketch, "E22.0.1.0", {"start": v(-140, -38) * mm, "end": v(-140, -58) * mm});
            skLineSegment(sketch, "E22.0.1.1", {"start": v(-140, -58) * mm, "end": v(-160, -58) * mm});
            skLineSegment(sketch, "E22.0.1.2", {"start": v(-150, -38) * mm, "end": v(-140, -38) * mm});
            skLineSegment(sketch, "E22.0.1.3", {"start": v(-150, -48) * mm, "end": v(-150, -38) * mm});
            skLineSegment(sketch, "E22.0.1.4", {"start": v(-160, -48) * mm, "end": v(-150, -48) * mm});
            skLineSegment(sketch, "E22.0.1.5", {"start": v(-160, -58) * mm, "end": v(-160, -48) * mm});
            skLineSegment(sketch, "E22.0.2.0", {"start": v(-140, 42) * mm, "end": v(-140, 22) * mm});
            skLineSegment(sketch, "E22.0.2.1", {"start": v(-140, 22) * mm, "end": v(-160, 22) * mm});
            skLineSegment(sketch, "E22.0.2.2", {"start": v(-150, 42) * mm, "end": v(-140, 42) * mm});
            skLineSegment(sketch, "E22.0.2.3", {"start": v(-150, 32) * mm, "end": v(-150, 42) * mm});
            skLineSegment(sketch, "E22.0.2.4", {"start": v(-160, 32) * mm, "end": v(-150, 32) * mm});
            skLineSegment(sketch, "E22.0.2.5", {"start": v(-160, 22) * mm, "end": v(-160, 32) * mm});
            skLineSegment(sketch, "E22.direction1", {"start": v(-160, -138) * mm, "end": v(-135, -138) * mm, "construction": true});
            skLineSegment(sketch, "E22.direction2", {"start": v(-160, -138) * mm, "end": v(-160, -58) * mm, "construction": true});
            skSolve(sketch);
        }
        {
            var Q0;
            Q0 = qSketchRegion(id + "F13", true);
            extrude(context, id + "F14", {"entities" : qUnion([Q0]), "operationType" : NewBodyOperationType.REMOVE, "oppositeDirection" : true, "depth" : 25 * mm});
        }
        {
            var Q0;
            {var subQ0=sQuery(id+"F0.wireOp",EDGE,"E2.top");Q0=makeQuery(id+"F12.boolean.opBoolean","MERGE",FACE,{"derivedFrom":[makeQuery(id+"F8.boolean.opBoolean","MERGE",FACE,{"derivedFrom":[makeQuery(id+"F4.boolean.opBoolean","MERGE",FACE,{"derivedFrom":[makeQuery(id+"F2.boolean.opBoolean","MERGE",FACE,{"derivedFrom":[makeQuery(id+"F1.opExtrude","CAP_FACE",FACE,{"disambiguationData":[OSD([sQuery(id+"F0.wireOp",EDGE,"E2.bottom"),subQ0,sQuery(id+"F0.wireOp",EDGE,"E2.left"),sQuery(id+"F0.wireOp",EDGE,"E2.right"),sQuery(id+"F0.wireOp",EDGE,"E3.bottom"),sQuery(id+"F0.wireOp",EDGE,"E3.top"),sQuery(id+"F0.wireOp",EDGE,"E3.left"),sQuery(id+"F0.wireOp",EDGE,"E3.right"),sQuery(id+"F0.wireOp",EDGE,"E4.0.1.0"),sQuery(id+"F0.wireOp",EDGE,"E4.0.1.1"),sQuery(id+"F0.wireOp",EDGE,"E4.0.1.2"),sQuery(id+"F0.wireOp",EDGE,"E4.0.1.3"),sQuery(id+"F0.wireOp",EDGE,"E4.0.2.0"),sQuery(id+"F0.wireOp",EDGE,"E4.0.2.1"),sQuery(id+"F0.wireOp",EDGE,"E4.0.2.2"),sQuery(id+"F0.wireOp",EDGE,"E4.0.2.3"),sQuery(id+"F0.wireOp",EDGE,"E4.0.3.0"),sQuery(id+"F0.wireOp",EDGE,"E4.0.3.1"),sQuery(id+"F0.wireOp",EDGE,"E4.0.3.2"),sQuery(id+"F0.wireOp",EDGE,"E4.0.3.3"),sQuery(id+"F0.wireOp",EDGE,"E4.1.0.0"),sQuery(id+"F0.wireOp",EDGE,"E4.1.0.1"),sQuery(id+"F0.wireOp",EDGE,"E4.1.0.2"),sQuery(id+"F0.wireOp",EDGE,"E4.1.0.3"),sQuery(id+"F0.wireOp",EDGE,"E4.1.1.0"),sQuery(id+"F0.wireOp",EDGE,"E4.1.1.1"),sQuery(id+"F0.wireOp",EDGE,"E4.1.1.2"),sQuery(id+"F0.wireOp",EDGE,"E4.1.1.3"),sQuery(id+"F0.wireOp",EDGE,"E4.1.2.0"),sQuery(id+"F0.wireOp",EDGE,"E4.1.2.1"),sQuery(id+"F0.wireOp",EDGE,"E4.1.2.2"),sQuery(id+"F0.wireOp",EDGE,"E4.1.2.3"),sQuery(id+"F0.wireOp",EDGE,"E4.1.3.0"),sQuery(id+"F0.wireOp",EDGE,"E4.1.3.1"),sQuery(id+"F0.wireOp",EDGE,"E4.1.3.2"),sQuery(id+"F0.wireOp",EDGE,"E4.1.3.3"),sQuery(id+"F0.wireOp",EDGE,"E4.2.0.0"),sQuery(id+"F0.wireOp",EDGE,"E4.2.0.1"),sQuery(id+"F0.wireOp",EDGE,"E4.2.0.2"),sQuery(id+"F0.wireOp",EDGE,"E4.2.0.3"),sQuery(id+"F0.wireOp",EDGE,"E4.2.1.0"),sQuery(id+"F0.wireOp",EDGE,"E4.2.1.1"),sQuery(id+"F0.wireOp",EDGE,"E4.2.1.2"),sQuery(id+"F0.wireOp",EDGE,"E4.2.1.3"),sQuery(id+"F0.wireOp",EDGE,"E4.2.2.0"),sQuery(id+"F0.wireOp",EDGE,"E4.2.2.1"),sQuery(id+"F0.wireOp",EDGE,"E4.2.2.2"),sQuery(id+"F0.wireOp",EDGE,"E4.2.2.3"),sQuery(id+"F0.wireOp",EDGE,"E4.2.3.0"),sQuery(id+"F0.wireOp",EDGE,"E4.2.3.1"),sQuery(id+"F0.wireOp",EDGE,"E4.2.3.2"),sQuery(id+"F0.wireOp",EDGE,"E4.2.3.3"),sQuery(id+"F0.wireOp",EDGE,"E4.3.0.0"),sQuery(id+"F0.wireOp",EDGE,"E4.3.0.1"),sQuery(id+"F0.wireOp",EDGE,"E4.3.0.2"),sQuery(id+"F0.wireOp",EDGE,"E4.3.0.3"),sQuery(id+"F0.wireOp",EDGE,"E4.3.1.0"),sQuery(id+"F0.wireOp",EDGE,"E4.3.1.1"),sQuery(id+"F0.wireOp",EDGE,"E4.3.1.2"),sQuery(id+"F0.wireOp",EDGE,"E4.3.1.3"),sQuery(id+"F0.wireOp",EDGE,"E4.3.2.0"),sQuery(id+"F0.wireOp",EDGE,"E4.3.2.1"),sQuery(id+"F0.wireOp",EDGE,"E4.3.2.2"),sQuery(id+"F0.wireOp",EDGE,"E4.3.2.3"),sQuery(id+"F0.wireOp",EDGE,"E4.3.3.0"),sQuery(id+"F0.wireOp",EDGE,"E4.3.3.1"),sQuery(id+"F0.wireOp",EDGE,"E4.3.3.2"),sQuery(id+"F0.wireOp",EDGE,"E4.3.3.3"),sQuery(id+"F0.wireOp",EDGE,"E4.4.0.0"),sQuery(id+"F0.wireOp",EDGE,"E4.4.0.1"),sQuery(id+"F0.wireOp",EDGE,"E4.4.0.2"),sQuery(id+"F0.wireOp",EDGE,"E4.4.0.3"),sQuery(id+"F0.wireOp",EDGE,"E4.4.1.0"),sQuery(id+"F0.wireOp",EDGE,"E4.4.1.1"),sQuery(id+"F0.wireOp",EDGE,"E4.4.1.2"),sQuery(id+"F0.wireOp",EDGE,"E4.4.1.3"),sQuery(id+"F0.wireOp",EDGE,"E4.4.2.0"),sQuery(id+"F0.wireOp",EDGE,"E4.4.2.1"),sQuery(id+"F0.wireOp",EDGE,"E4.4.2.2"),sQuery(id+"F0.wireOp",EDGE,"E4.4.2.3"),sQuery(id+"F0.wireOp",EDGE,"E4.4.3.0"),sQuery(id+"F0.wireOp",EDGE,"E4.4.3.1"),sQuery(id+"F0.wireOp",EDGE,"E4.4.3.2"),sQuery(id+"F0.wireOp",EDGE,"E4.4.3.3")])],"isStart":false}),makeQuery(id+"F2.opExtrude","SWEPT_FACE",FACE,{"disambiguationData":[OSD([subQ0]),TDD([makeQuery(id+"F1.opExtrude","CAP_EDGE",EDGE,{"disambiguationData":[OSD([subQ0])],"isStart":false})])]})]}),makeQuery(id+"F4.opExtrude","SWEPT_FACE",FACE,{"disambiguationData":[OSD([sQuery(id+"F3.wireOp",EDGE,"E5.bottom")])]})]}),makeQuery(id+"F8.opExtrude","SWEPT_FACE",FACE,{"disambiguationData":[OSD([sQuery(id+"F7.wireOp",EDGE,"E10.bottom")])]})]}),makeQuery(id+"F12.opExtrude","SWEPT_FACE",FACE,{"disambiguationData":[OSD([sQuery(id+"F11.wireOp",EDGE,"E15.bottom")])]})]});}
            var sketch = newSketch(context, id + "F15", { "sketchPlane" : qUnion([Q0])});
            skLineSegment(sketch, "E23", {"start": v(-176.3, -116.5) * mm, "end": v(160.59, -116.5) * mm, "construction": true});
            skCircle(sketch, "E24", {"center": v(100, -116.5) * mm, "radius": 7.05 * mm});
            skCircle(sketch, "E25.1.0.0", {"center": v(50, -116.5) * mm, "radius": 7.05 * mm});
            skCircle(sketch, "E25.2.0.0", {"center": v(0, -116.5) * mm, "radius": 7.05 * mm});
            skCircle(sketch, "E25.3.0.0", {"center": v(-50, -116.5) * mm, "radius": 7.05 * mm});
            skCircle(sketch, "E25.4.0.0", {"center": v(-100, -116.5) * mm, "radius": 7.05 * mm});
            skLineSegment(sketch, "E25.direction1", {"start": v(100, -116.5) * mm, "end": v(50, -116.5) * mm, "construction": true});
            skSolve(sketch);
        }
        {
            var Q0;
            Q0 = qSketchRegion(id + "F15", true);
            extrude(context, id + "F16", {"entities" : qUnion([Q0]), "operationType" : NewBodyOperationType.ADD, "depth" : 3 * mm});
        }
    });
